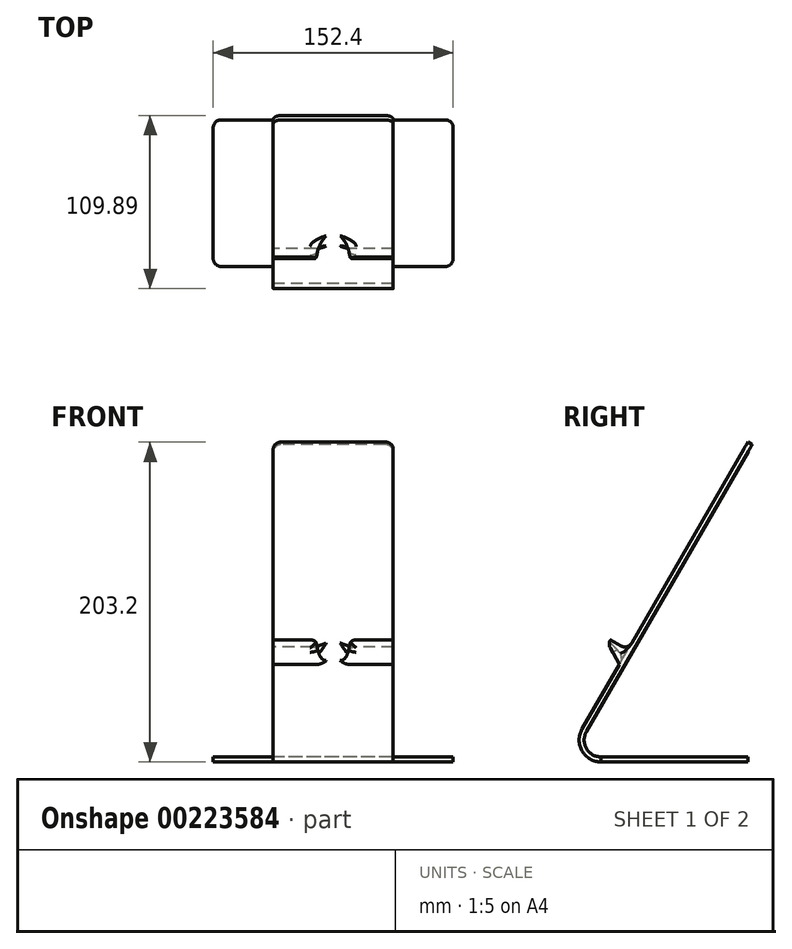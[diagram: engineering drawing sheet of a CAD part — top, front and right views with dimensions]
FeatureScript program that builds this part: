
annotation { "Feature Type Name" : "Feature", "Feature Type Description" : "" }
export const myFeature = defineFeature(function(context is Context, id is Id, definition is map)
    precondition{}
    {
        {
            var Q0;
            Q0=qCreatedBy(makeId("Right.planeOp"),FACE);
            var sketch = newSketch(context, id + "F0", { "sketchPlane" : qUnion([Q0])});
            skLineSegment(sketch, "E0", {"start": v(17.96, 0) * mm, "end": v(-75.26, 0) * mm});
            skArc(sketch, "E1", {"start": v(-87.31, 20.87) * mm, "mid": v(-87.31, 6.96) * mm, "end": v(-75.26, 0) * mm});
            skLineSegment(sketch, "E2", {"start": v(-58.24, 71.22) * mm, "end": v(-69.24, 77.57) * mm});
            skLineSegment(sketch, "E3.0", {"start": v(-84.56, 19.28) * mm, "end": v(20.7, 201.61) * mm});
            skArc(sketch, "E3.1", {"start": v(-84.56, 19.28) * mm, "mid": v(-84.56, 8.54) * mm, "end": v(-75.26, 3.17) * mm});
            skLineSegment(sketch, "E3.2", {"start": v(17.96, 3.18) * mm, "end": v(-75.26, 3.17) * mm});
            skLineSegment(sketch, "E4", {"start": v(17.96, 3.18) * mm, "end": v(17.96, 0) * mm});
            skLineSegment(sketch, "E5", {"start": v(20.7, 201.61) * mm, "end": v(17.96, 203.2) * mm});
            skLineSegment(sketch, "E6.0", {"start": v(-59.83, 68.47) * mm, "end": v(-70.83, 74.82) * mm});
            skLineSegment(sketch, "E7", {"start": v(-69.24, 77.57) * mm, "end": v(-70.83, 74.82) * mm});
            skLineSegment(sketch, "E8", {"start": v(-87.31, 20.87) * mm, "end": v(-59.83, 68.47) * mm});
            skLineSegment(sketch, "E9", {"start": v(-58.24, 71.22) * mm, "end": v(17.96, 203.2) * mm});
            skSolve(sketch);
        }
        {
            var Q0;
            Q0=makeQuery(id+"F0.imprint","IMPRINT",FACE,{"disambiguationData":[TD([[makeQuery(id+"F0.imprint","IMPRINT",EDGE,{"derivedFrom":sQuery(id+"F0.wireOp",EDGE,"E0")}),-1.0]])]});
            var Q1;
            {var subQ0=sQuery(id+"F0.wireOp",EDGE,"E2");Q1=makeQuery(id+"F0.imprint","IMPRINT",FACE,{"disambiguationData":[TD([[makeQuery(id+"F0.imprint","IMPRINT",EDGE,{"derivedFrom":subQ0}),1.0]])]});}
            extrude(context, id + "F1", {"entities" : qUnion([Q0, Q1]), "depth" : 38.1 * mm, "hasSecondDirection" : true, "secondDirectionOppositeDirection" : true, "secondDirectionDepth" : 38.1 * mm});
        }
        {
            var Q0;
            Q0=makeQuery(id+"F1.opExtrude","SWEPT_FACE",FACE,{"disambiguationData":[OSD([sQuery(id+"F0.wireOp",EDGE,"E2")])]});
            var sketch = newSketch(context, id + "F2", { "sketchPlane" : qUnion([Q0])});
            skLineSegment(sketch, "E10", {"start": v(0, -98.75) * mm, "end": v(0, -86.05) * mm, "construction": true});
            skLineSegment(sketch, "E11.bottom", {"start": v(-9.52, -98.75) * mm, "end": v(9.53, -98.75) * mm});
            skLineSegment(sketch, "E11.top", {"start": v(-9.52, -86.05) * mm, "end": v(9.53, -86.05) * mm});
            skLineSegment(sketch, "E11.left", {"start": v(-9.52, -98.75) * mm, "end": v(-9.52, -86.05) * mm});
            skLineSegment(sketch, "E11.right", {"start": v(9.53, -98.75) * mm, "end": v(9.53, -86.05) * mm});
            skPoint(sketch, "E11.middle", {"position": v(0, -92.4) * mm});
            skSolve(sketch);
        }
        {
            var Q0;
            Q0 = qSketchRegion(id + "F2", true);
            var Q1;
            Q1=makeQuery(id+"F1.opExtrude","SWEPT_FACE",FACE,{"disambiguationData":[OSD([sQuery(id+"F0.wireOp",EDGE,"E6.0")])]});
            extrude(context, id + "F3", {"entities" : qUnion([Q0]), "operationType" : NewBodyOperationType.REMOVE, "endBound" : BoundingType.UP_TO_SURFACE, "oppositeDirection" : true, "endBoundEntityFace" : qUnion([Q1]), "depth" : 25.4 * mm});
        }
        {
            var Q0;
            {var subQ1=sQuery(id+"F0.wireOp",EDGE,"E8");var subQ2=sQuery(id+"F0.wireOp",EDGE,"E6.0");Q0=makeQuery(id+"F3.boolean.opBoolean","SPLIT",EDGE,{"disambiguationData":[TD([makeQuery(id+"F3.opExtrude","SWEPT_FACE",FACE,{"disambiguationData":[OSD([sQuery(id+"F2.wireOp",EDGE,"E11.right")])]})])],"derivedFrom":makeQuery(id+"F1.opExtrude","SWEPT_EDGE",EDGE,{"disambiguationData":[OSD([subQ2,subQ1])]})});}
            var Q1;
            {var subQ1=sQuery(id+"F0.wireOp",EDGE,"E8");var subQ2=sQuery(id+"F0.wireOp",EDGE,"E6.0");Q1=makeQuery(id+"F3.boolean.opBoolean","SPLIT",EDGE,{"disambiguationData":[TD([makeQuery(id+"F3.opExtrude","SWEPT_FACE",FACE,{"disambiguationData":[OSD([sQuery(id+"F2.wireOp",EDGE,"E11.left")])]})])],"derivedFrom":makeQuery(id+"F1.opExtrude","SWEPT_EDGE",EDGE,{"disambiguationData":[OSD([subQ2,subQ1])]})});}
            chamfer(context, id + "F4", {"entities" : qUnion([Q0, Q1]), "chamferType" : ChamferType.TWO_OFFSETS, "width1" : 7.62 * mm, "oppositeDirection" : false, "width2" : 12.7 * mm, "tangentPropagation" : true});
        }
        {
            var Q0;
            {var subQ0=sQuery(id+"F0.wireOp",EDGE,"E9");var subQ2=sQuery(id+"F0.wireOp",EDGE,"E2");Q0=makeQuery(id+"F3.boolean.opBoolean","SPLIT",EDGE,{"disambiguationData":[TD([makeQuery(id+"F3.opExtrude","SWEPT_FACE",FACE,{"disambiguationData":[OSD([sQuery(id+"F2.wireOp",EDGE,"E11.left")])]})])],"derivedFrom":makeQuery(id+"F1.opExtrude","SWEPT_EDGE",EDGE,{"disambiguationData":[OSD([subQ2,subQ0])]})});}
            var Q1;
            {var subQ0=sQuery(id+"F0.wireOp",EDGE,"E9");var subQ2=sQuery(id+"F0.wireOp",EDGE,"E2");Q1=makeQuery(id+"F3.boolean.opBoolean","SPLIT",EDGE,{"disambiguationData":[TD([makeQuery(id+"F3.opExtrude","SWEPT_FACE",FACE,{"disambiguationData":[OSD([sQuery(id+"F2.wireOp",EDGE,"E11.right")])]})])],"derivedFrom":makeQuery(id+"F1.opExtrude","SWEPT_EDGE",EDGE,{"disambiguationData":[OSD([subQ2,subQ0])]})});}
            fillet(context, id + "F5", {"entities" : qUnion([Q0, Q1]), "radius" : 5.08 * mm, "tangentPropagation" : true, "allowEdgeOverflow" : false});
        }
        {
            var Q0;
            Q0=makeQuery(id+"F3.boolean.opBoolean","COPY",EDGE,{"derivedFrom":makeQuery(id+"F3.opExtrude","SWEPT_EDGE",EDGE,{"disambiguationData":[OSD([sQuery(id+"F0.wireOp",EDGE,"E2"),sQuery(id+"F0.wireOp",EDGE,"E9"),sQuery(id+"F2.wireOp",EDGE,"E11.top"),sQuery(id+"F2.wireOp",EDGE,"E11.left")])]})});
            var Q1;
            Q1=makeQuery(id+"F3.boolean.opBoolean","COPY",EDGE,{"derivedFrom":makeQuery(id+"F3.opExtrude","SWEPT_EDGE",EDGE,{"disambiguationData":[OSD([sQuery(id+"F0.wireOp",EDGE,"E2"),sQuery(id+"F0.wireOp",EDGE,"E9"),sQuery(id+"F2.wireOp",EDGE,"E11.top"),sQuery(id+"F2.wireOp",EDGE,"E11.right")])]})});
            fillet(context, id + "F6", {"entities" : qUnion([Q0, Q1]), "radius" : 5.08 * mm, "tangentPropagation" : true, "allowEdgeOverflow" : false});
        }
        {
            var Q0;
            {var subQ0=sQuery(id+"F0.wireOp",EDGE,"E9");var subQ1=sQuery(id+"F0.wireOp",EDGE,"E8");var subQ2=sQuery(id+"F0.wireOp",EDGE,"E6.0");var subQ3=sQuery(id+"F0.wireOp",EDGE,"E2");var subQ4=sQuery(id+"F2.wireOp",EDGE,"E11.top");var subQ5=sQuery(id+"F2.wireOp",EDGE,"E11.left");Q0=makeQuery(id+"F6.opFillet","BLEND_EDGE",EDGE,{"blendedFrom":[makeQuery(id+"F3.boolean.opBoolean","COPY",EDGE,{"derivedFrom":makeQuery(id+"F3.opExtrude","SWEPT_EDGE",EDGE,{"disambiguationData":[OSD([subQ3,subQ0,subQ4,subQ5])]})}),makeQuery(id+"F4.opChamfer","BLEND_FACE",FACE,{"disambiguationData":[OSD([subQ2,subQ1]),TDD([makeQuery(id+"F3.boolean.opBoolean","SPLIT",EDGE,{"disambiguationData":[TD([makeQuery(id+"F3.opExtrude","SWEPT_FACE",FACE,{"disambiguationData":[OSD([subQ5])]})])],"derivedFrom":makeQuery(id+"F1.opExtrude","SWEPT_EDGE",EDGE,{"disambiguationData":[OSD([subQ2,subQ1])]})})])]})],"blendedInto":[makeQuery(id+"F4.opChamfer","BLEND_FACE",FACE,{"disambiguationData":[OSD([subQ2,subQ1]),TDD([makeQuery(id+"F3.boolean.opBoolean","SPLIT",EDGE,{"disambiguationData":[TD([makeQuery(id+"F3.opExtrude","SWEPT_FACE",FACE,{"disambiguationData":[OSD([subQ5])]})])],"derivedFrom":makeQuery(id+"F1.opExtrude","SWEPT_EDGE",EDGE,{"disambiguationData":[OSD([subQ2,subQ1])]})})])]})]});}
            var Q1;
            {var subQ0=sQuery(id+"F0.wireOp",EDGE,"E9");var subQ2=sQuery(id+"F0.wireOp",EDGE,"E2");var subQ3=sQuery(id+"F2.wireOp",EDGE,"E11.top");var subQ4=sQuery(id+"F2.wireOp",EDGE,"E11.left");Q1=makeQuery(id+"F6.opFillet","BLEND_EDGE",EDGE,{"blendedFrom":[makeQuery(id+"F3.boolean.opBoolean","COPY",EDGE,{"derivedFrom":makeQuery(id+"F3.opExtrude","SWEPT_EDGE",EDGE,{"disambiguationData":[OSD([subQ2,subQ0,subQ3,subQ4])]})}),makeQuery(id+"F5.opFillet","BLEND_FACE",FACE,{"disambiguationData":[OSD([subQ2,subQ0]),TDD([makeQuery(id+"F3.boolean.opBoolean","SPLIT",EDGE,{"disambiguationData":[TD([makeQuery(id+"F3.opExtrude","SWEPT_FACE",FACE,{"disambiguationData":[OSD([subQ4])]})])],"derivedFrom":makeQuery(id+"F1.opExtrude","SWEPT_EDGE",EDGE,{"disambiguationData":[OSD([subQ2,subQ0])]})})])]})],"blendedInto":[makeQuery(id+"F5.opFillet","BLEND_FACE",FACE,{"disambiguationData":[OSD([subQ2,subQ0]),TDD([makeQuery(id+"F3.boolean.opBoolean","SPLIT",EDGE,{"disambiguationData":[TD([makeQuery(id+"F3.opExtrude","SWEPT_FACE",FACE,{"disambiguationData":[OSD([subQ4])]})])],"derivedFrom":makeQuery(id+"F1.opExtrude","SWEPT_EDGE",EDGE,{"disambiguationData":[OSD([subQ2,subQ0])]})})])]})]});}
            var Q2;
            {var subQ0=sQuery(id+"F0.wireOp",EDGE,"E9");var subQ1=sQuery(id+"F0.wireOp",EDGE,"E8");var subQ2=sQuery(id+"F0.wireOp",EDGE,"E6.0");var subQ3=sQuery(id+"F0.wireOp",EDGE,"E2");var subQ4=sQuery(id+"F2.wireOp",EDGE,"E11.top");var subQ5=sQuery(id+"F2.wireOp",EDGE,"E11.right");Q2=makeQuery(id+"F6.opFillet","BLEND_EDGE",EDGE,{"blendedFrom":[makeQuery(id+"F3.boolean.opBoolean","COPY",EDGE,{"derivedFrom":makeQuery(id+"F3.opExtrude","SWEPT_EDGE",EDGE,{"disambiguationData":[OSD([subQ3,subQ0,subQ4,subQ5])]})}),makeQuery(id+"F4.opChamfer","BLEND_FACE",FACE,{"disambiguationData":[OSD([subQ2,subQ1]),TDD([makeQuery(id+"F3.boolean.opBoolean","SPLIT",EDGE,{"disambiguationData":[TD([makeQuery(id+"F3.opExtrude","SWEPT_FACE",FACE,{"disambiguationData":[OSD([subQ5])]})])],"derivedFrom":makeQuery(id+"F1.opExtrude","SWEPT_EDGE",EDGE,{"disambiguationData":[OSD([subQ2,subQ1])]})})])]})],"blendedInto":[makeQuery(id+"F4.opChamfer","BLEND_FACE",FACE,{"disambiguationData":[OSD([subQ2,subQ1]),TDD([makeQuery(id+"F3.boolean.opBoolean","SPLIT",EDGE,{"disambiguationData":[TD([makeQuery(id+"F3.opExtrude","SWEPT_FACE",FACE,{"disambiguationData":[OSD([subQ5])]})])],"derivedFrom":makeQuery(id+"F1.opExtrude","SWEPT_EDGE",EDGE,{"disambiguationData":[OSD([subQ2,subQ1])]})})])]})]});}
            var Q3;
            {var subQ0=sQuery(id+"F0.wireOp",EDGE,"E9");var subQ2=sQuery(id+"F0.wireOp",EDGE,"E2");var subQ3=sQuery(id+"F2.wireOp",EDGE,"E11.top");var subQ4=sQuery(id+"F2.wireOp",EDGE,"E11.right");Q3=makeQuery(id+"F6.opFillet","BLEND_EDGE",EDGE,{"blendedFrom":[makeQuery(id+"F3.boolean.opBoolean","COPY",EDGE,{"derivedFrom":makeQuery(id+"F3.opExtrude","SWEPT_EDGE",EDGE,{"disambiguationData":[OSD([subQ2,subQ0,subQ3,subQ4])]})}),makeQuery(id+"F5.opFillet","BLEND_FACE",FACE,{"disambiguationData":[OSD([subQ2,subQ0]),TDD([makeQuery(id+"F3.boolean.opBoolean","SPLIT",EDGE,{"disambiguationData":[TD([makeQuery(id+"F3.opExtrude","SWEPT_FACE",FACE,{"disambiguationData":[OSD([subQ4])]})])],"derivedFrom":makeQuery(id+"F1.opExtrude","SWEPT_EDGE",EDGE,{"disambiguationData":[OSD([subQ2,subQ0])]})})])]})],"blendedInto":[makeQuery(id+"F5.opFillet","BLEND_FACE",FACE,{"disambiguationData":[OSD([subQ2,subQ0]),TDD([makeQuery(id+"F3.boolean.opBoolean","SPLIT",EDGE,{"disambiguationData":[TD([makeQuery(id+"F3.opExtrude","SWEPT_FACE",FACE,{"disambiguationData":[OSD([subQ4])]})])],"derivedFrom":makeQuery(id+"F1.opExtrude","SWEPT_EDGE",EDGE,{"disambiguationData":[OSD([subQ2,subQ0])]})})])]})]});}
            fillet(context, id + "F7", {"entities" : qUnion([Q0, Q1, Q2, Q3]), "radius" : 5.08 * mm, "tangentPropagation" : true, "allowEdgeOverflow" : false});
        }
        {
            var Q0;
            {var subQ1=sQuery(id+"F0.wireOp",EDGE,"E8");var subQ2=sQuery(id+"F0.wireOp",EDGE,"E7");var subQ3=sQuery(id+"F0.wireOp",EDGE,"E6.0");var subQ6=makeQuery(id+"F3.opExtrude","SWEPT_FACE",FACE,{"disambiguationData":[OSD([sQuery(id+"F2.wireOp",EDGE,"E11.left")])]});Q0=makeQuery(id+"F4.opChamfer","BLEND_EDGE",EDGE,{"blendedFrom":[makeQuery(id+"F3.boolean.opBoolean","SPLIT",EDGE,{"disambiguationData":[TD([subQ6])],"derivedFrom":makeQuery(id+"F1.opExtrude","SWEPT_EDGE",EDGE,{"disambiguationData":[OSD([subQ3,subQ1])]})}),makeQuery(id+"F3.boolean.opBoolean","SPLIT",FACE,{"disambiguationData":[TD([subQ6])],"derivedFrom":makeQuery(id+"F1.opExtrude","SWEPT_FACE",FACE,{"disambiguationData":[OSD([subQ2])]})})],"blendedInto":[makeQuery(id+"F3.boolean.opBoolean","SPLIT",FACE,{"disambiguationData":[TD([subQ6])],"derivedFrom":makeQuery(id+"F1.opExtrude","SWEPT_FACE",FACE,{"disambiguationData":[OSD([subQ2])]})})]});}
            var Q1;
            {var subQ1=sQuery(id+"F0.wireOp",EDGE,"E8");var subQ2=sQuery(id+"F0.wireOp",EDGE,"E7");var subQ3=sQuery(id+"F0.wireOp",EDGE,"E6.0");var subQ6=makeQuery(id+"F3.opExtrude","SWEPT_FACE",FACE,{"disambiguationData":[OSD([sQuery(id+"F2.wireOp",EDGE,"E11.right")])]});Q1=makeQuery(id+"F4.opChamfer","BLEND_EDGE",EDGE,{"blendedFrom":[makeQuery(id+"F3.boolean.opBoolean","SPLIT",EDGE,{"disambiguationData":[TD([subQ6])],"derivedFrom":makeQuery(id+"F1.opExtrude","SWEPT_EDGE",EDGE,{"disambiguationData":[OSD([subQ3,subQ1])]})}),makeQuery(id+"F3.boolean.opBoolean","SPLIT",FACE,{"disambiguationData":[TD([subQ6])],"derivedFrom":makeQuery(id+"F1.opExtrude","SWEPT_FACE",FACE,{"disambiguationData":[OSD([subQ2])]})})],"blendedInto":[makeQuery(id+"F3.boolean.opBoolean","SPLIT",FACE,{"disambiguationData":[TD([subQ6])],"derivedFrom":makeQuery(id+"F1.opExtrude","SWEPT_FACE",FACE,{"disambiguationData":[OSD([subQ2])]})})]});}
            fillet(context, id + "F8", {"entities" : qUnion([Q0, Q1]), "radius" : 5.08 * mm, "tangentPropagation" : true, "allowEdgeOverflow" : false});
        }
        {
            var Q0;
            Q0=makeQuery(id+"F1.opExtrude","CAP_FACE",FACE,{"disambiguationData":[OSD([sQuery(id+"F0.wireOp",EDGE,"E0"),sQuery(id+"F0.wireOp",EDGE,"E1"),sQuery(id+"F0.wireOp",EDGE,"E2"),sQuery(id+"F0.wireOp",EDGE,"E3.0"),sQuery(id+"F0.wireOp",EDGE,"E3.1"),sQuery(id+"F0.wireOp",EDGE,"E3.2"),sQuery(id+"F0.wireOp",EDGE,"E4"),sQuery(id+"F0.wireOp",EDGE,"E5"),sQuery(id+"F0.wireOp",EDGE,"E6.0"),sQuery(id+"F0.wireOp",EDGE,"E7"),sQuery(id+"F0.wireOp",EDGE,"E8"),sQuery(id+"F0.wireOp",EDGE,"E9")])],"isStart":true});
            var sketch = newSketch(context, id + "F9", { "sketchPlane" : qUnion([Q0])});
            skLineSegment(sketch, "E12", {"start": v(75.26, 3.17) * mm, "end": v(75.26, 0) * mm});
            skLineSegment(sketch, "E13", {"start": v(75.26, 0) * mm, "end": v(-17.96, 0) * mm});
            skLineSegment(sketch, "E14", {"start": v(-17.96, 0) * mm, "end": v(-17.96, 3.18) * mm});
            skLineSegment(sketch, "E15", {"start": v(-17.96, 3.18) * mm, "end": v(75.26, 3.17) * mm});
            skSolve(sketch);
        }
        {
            var Q0;
            Q0=makeQuery(id+"F9.imprint","IMPRINT",FACE,{"disambiguationData":[TD([[makeQuery(id+"F9.imprint","IMPRINT",EDGE,{"derivedFrom":sQuery(id+"F9.wireOp",EDGE,"E12")}),-1.0]])]});
            extrude(context, id + "F10", {"entities" : qUnion([Q0]), "operationType" : NewBodyOperationType.ADD, "depth" : 38.1 * mm});
        }
        {
            var Q0;
            Q0=makeQuery(id+"F10.opExtrude","CAP_EDGE",EDGE,{"disambiguationData":[OSD([sQuery(id+"F9.wireOp",EDGE,"E14")])],"isStart":false});
            var Q1;
            Q1=makeQuery(id+"F10.opExtrude","CAP_EDGE",EDGE,{"disambiguationData":[OSD([sQuery(id+"F9.wireOp",EDGE,"E12")])],"isStart":false});
            var Q2;
            Q2=makeQuery(id+"F10.opExtrude","CAP_EDGE",EDGE,{"disambiguationData":[OSD([sQuery(id+"F9.wireOp",EDGE,"E12")])],"isStart":true});
            fillet(context, id + "F11", {"entities" : qUnion([Q0, Q1, Q2]), "radius" : 5.08 * mm, "tangentPropagation" : true, "allowEdgeOverflow" : false});
        }
        {
            var Q0;
            Q0=makeQuery(id+"F1.opExtrude","SWEPT_BODY",BODY,{"disambiguationData":[OSD([sQuery(id+"F0.wireOp",EDGE,"E0"),sQuery(id+"F0.wireOp",EDGE,"E1"),sQuery(id+"F0.wireOp",EDGE,"E2"),sQuery(id+"F0.wireOp",EDGE,"E3.0"),sQuery(id+"F0.wireOp",EDGE,"E3.1"),sQuery(id+"F0.wireOp",EDGE,"E3.2"),sQuery(id+"F0.wireOp",EDGE,"E4"),sQuery(id+"F0.wireOp",EDGE,"E5"),sQuery(id+"F0.wireOp",EDGE,"E6.0"),sQuery(id+"F0.wireOp",EDGE,"E7"),sQuery(id+"F0.wireOp",EDGE,"E8"),sQuery(id+"F0.wireOp",EDGE,"E9")])]});
            var Q1;
            Q1=qCreatedBy(makeId("Right.planeOp"),FACE);
            mirror(context, id + "F12", {"operationType" : NewBodyOperationType.ADD, "entities" : qUnion([Q0]), "mirrorPlane" : qUnion([Q1])});
        }
        {
            var Q0;
            Q0=makeQuery(id+"F1.opExtrude","CAP_EDGE",EDGE,{"disambiguationData":[OSD([sQuery(id+"F0.wireOp",EDGE,"E5")])],"isStart":true});
            var Q1;
            Q1=makeQuery(id+"F1.opExtrude","CAP_EDGE",EDGE,{"disambiguationData":[OSD([sQuery(id+"F0.wireOp",EDGE,"E5")])],"isStart":false});
            fillet(context, id + "F13", {"entities" : qUnion([Q0, Q1]), "radius" : 5.08 * mm, "tangentPropagation" : true, "allowEdgeOverflow" : false});
        }
    });
